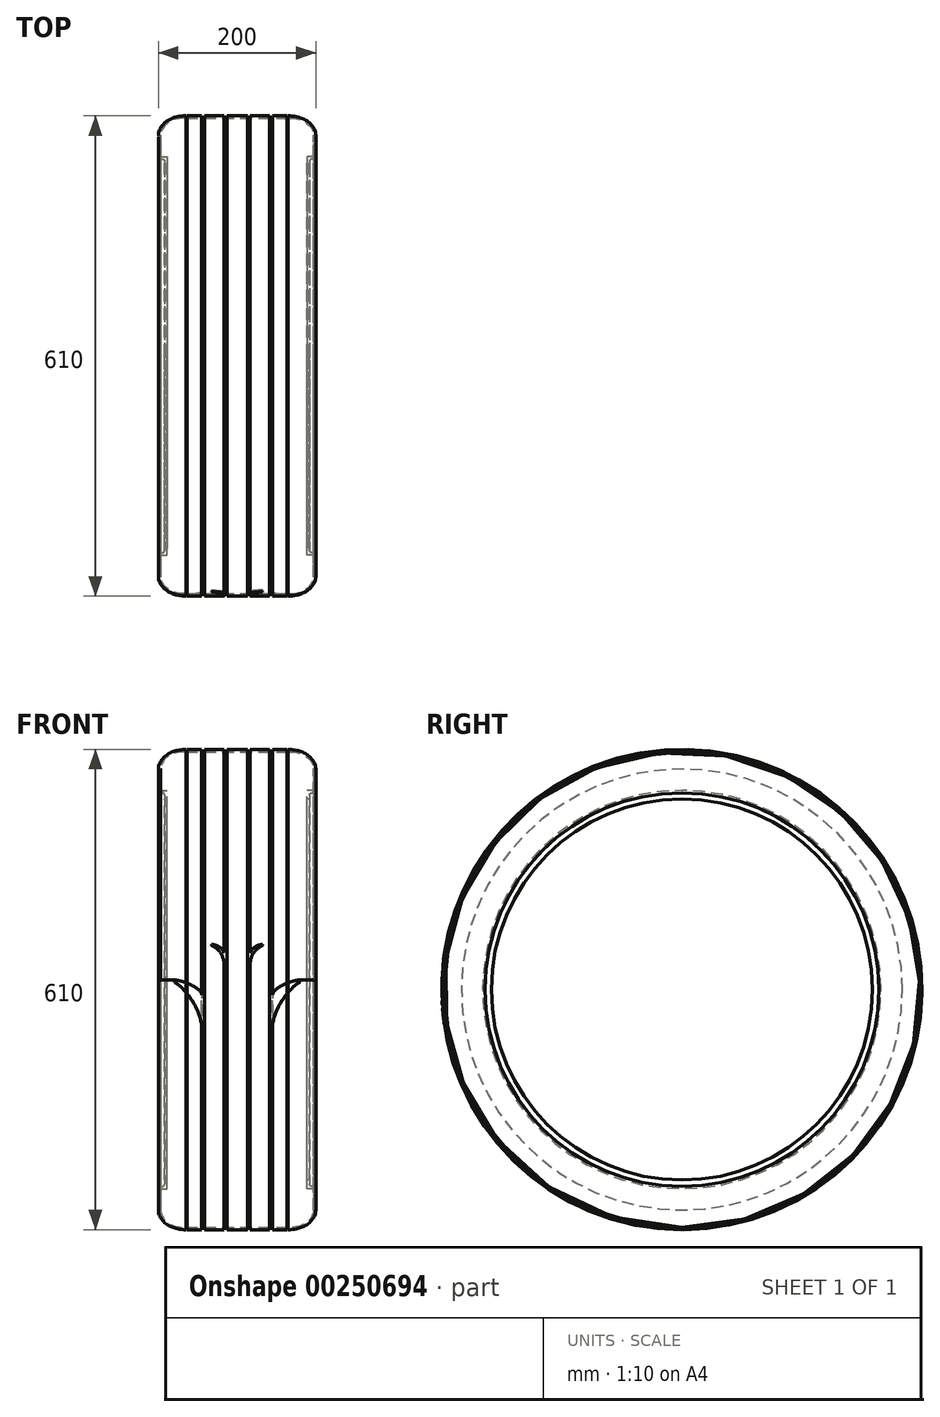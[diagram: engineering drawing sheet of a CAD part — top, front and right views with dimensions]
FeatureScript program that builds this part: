
annotation { "Feature Type Name" : "Feature", "Feature Type Description" : "" }
export const myFeature = defineFeature(function(context is Context, id is Id, definition is map)
    precondition{}
    {
        {
            var Q0;
            Q0=qCreatedBy(makeId("Front.planeOp"),FACE);
            var sketch = newSketch(context, id + "F0", { "sketchPlane" : qUnion([Q0])});
            skLineSegment(sketch, "E0", {"start": v(0, 302) * mm, "end": v(0, 305) * mm});
            skLineSegment(sketch, "E1", {"start": v(0, 305) * mm, "end": v(-65, 305) * mm});
            skLineSegment(sketch, "E2", {"start": v(-92, 250) * mm, "end": v(-100, 250) * mm});
            skLineSegment(sketch, "E3", {"start": v(-100, 250) * mm, "end": v(-100, 280) * mm});
            skFitSpline(sketch, "E4", {"points": [v(-100, 280) * mm, v(-65, 305) * mm], "startDerivative": vector(0, 35.86) * mm, "endDerivative": vector(66.84, 0) * mm});
            skLineSegment(sketch, "E5.0", {"start": v(0, 302) * mm, "end": v(-65, 302) * mm});
            skFitSpline(sketch, "E6.0", {"points": [v(-97, 280) * mm, v(-97, 281.23) * mm, v(-96.67, 283.74) * mm, v(-94.69, 288.83) * mm, v(-89.66, 294.94) * mm, v(-79.59, 300.46) * mm, v(-70.28, 302) * mm, v(-65, 302) * mm]});
            skLineSegment(sketch, "E7.0", {"start": v(-89, 253) * mm, "end": v(-97, 253) * mm});
            skLineSegment(sketch, "E8", {"start": v(-92, 250) * mm, "end": v(-92, 242) * mm});
            skLineSegment(sketch, "E9", {"start": v(-89, 253) * mm, "end": v(-89, 242) * mm});
            skLineSegment(sketch, "E10", {"start": v(-97, 280) * mm, "end": v(-97, 253) * mm});
            skLineSegment(sketch, "E11", {"start": v(-92, 242) * mm, "end": v(-89, 242) * mm});
            skLineSegment(sketch, "E12", {"start": v(0, 0) * mm, "end": v(-100, 0) * mm, "construction": true});
            skSolve(sketch);
        }
        {
            var Q0;
            Q0=makeQuery(id+"F0.imprint","IMPRINT",FACE,{"disambiguationData":[TD([[makeQuery(id+"F0.imprint","IMPRINT",EDGE,{"derivedFrom":sQuery(id+"F0.wireOp",EDGE,"E0")}),1.0]])]});
            var Q1;
            Q1=sQuery(id+"F0.wireOp",EDGE,"E12");
            revolve(context, id + "F1", {"entities" : qUnion([Q0]), "axis" : qUnion([Q1]), "revolveType" : RevolveType.FULL});
        }
        {
            var Q0;
            Q0=qCreatedBy(makeId("Front.planeOp"),FACE);
            var sketch = newSketch(context, id + "F2", { "sketchPlane" : qUnion([Q0])});
            skLineSegment(sketch, "E13.bottom", {"start": v(-16.5, 310) * mm, "end": v(-13, 310) * mm});
            skLineSegment(sketch, "E13.top", {"start": v(-16.5, 303) * mm, "end": v(-13, 303) * mm});
            skLineSegment(sketch, "E13.left", {"start": v(-16.5, 310) * mm, "end": v(-16.5, 303) * mm});
            skLineSegment(sketch, "E13.right", {"start": v(-13, 310) * mm, "end": v(-13, 303) * mm});
            skLineSegment(sketch, "E14.bottom", {"start": v(-45, 310) * mm, "end": v(-41.5, 310) * mm});
            skLineSegment(sketch, "E14.top", {"start": v(-45, 303) * mm, "end": v(-41.5, 303) * mm});
            skLineSegment(sketch, "E14.left", {"start": v(-45, 310) * mm, "end": v(-45, 303) * mm});
            skLineSegment(sketch, "E14.right", {"start": v(-41.5, 310) * mm, "end": v(-41.5, 303) * mm});
            skSolve(sketch);
        }
        {
            var Q0;
            Q0=qSketchRegion(id+"F2",true);
            var Q1;
            Q1=sQuery(id+"F0.wireOp",EDGE,"E12");
            revolve(context, id + "F3", {"operationType" : NewBodyOperationType.REMOVE, "entities" : qUnion([Q0]), "axis" : qUnion([Q1]), "revolveType" : RevolveType.FULL, "oppositeDirection" : true});
        }
        {
            var Q0;
            Q0=qCreatedBy(makeId("Front.planeOp"),FACE);
            cPlane(context, id + "F4", {"entities" : qUnion([Q0]), "cplaneType" : CPlaneType.OFFSET, "offset" : 350 * mm, "width" : 150 * mm, "height" : 150 * mm});
        }
        {
            var Q0;
            Q0=qCreatedBy(id+"F4.planeOp",FACE);
            var sketch = newSketch(context, id + "F5", { "sketchPlane" : qUnion([Q0])});
            skLineSegment(sketch, "E15", {"start": v(-45, -7) * mm, "end": v(-45, -45) * mm});
            skLineSegment(sketch, "E16", {"start": v(-85, 13) * mm, "end": v(-85, 11.5) * mm});
            skFitSpline(sketch, "E17", {"points": [v(-85, 11.5) * mm, v(-45, -45) * mm], "startDerivative": vector(44.6, -10.96) * mm, "endDerivative": vector(11.18, -76.38) * mm});
            skFitSpline(sketch, "E18", {"points": [v(-85, 13) * mm, v(-45, -7) * mm], "startDerivative": vector(39, 0) * mm, "endDerivative": vector(0, -30) * mm});
            skLineSegment(sketch, "E19", {"start": v(-16.5, 32) * mm, "end": v(-16.5, 47) * mm});
            skLineSegment(sketch, "E20", {"start": v(-32.5, 57.5) * mm, "end": v(-32.5, 56) * mm});
            skArc(sketch, "E21", {"start": v(-16.5, 32) * mm, "mid": v(-20.87, 46.42) * mm, "end": v(-32.5, 56) * mm});
            skFitSpline(sketch, "E22", {"points": [v(-16.5, 47) * mm, v(-32.5, 57.5) * mm], "startDerivative": vector(-6, 19.5) * mm, "endDerivative": vector(-15, 0) * mm});
            skSolve(sketch);
        }
        {
            var Q0;
            Q0=makeQuery(id+"F5.imprint","IMPRINT",FACE,{"disambiguationData":[TD([[makeQuery(id+"F5.imprint","IMPRINT",EDGE,{"derivedFrom":sQuery(id+"F5.wireOp",EDGE,"E15")}),-1.0]])]});
            var Q1;
            Q1=makeQuery(id+"F5.imprint","IMPRINT",FACE,{"disambiguationData":[TD([[makeQuery(id+"F5.imprint","IMPRINT",EDGE,{"derivedFrom":sQuery(id+"F5.wireOp",EDGE,"E19")}),1.0]])]});
            var Q2;
            Q2=makeQuery(id+"F3.boolean.opBoolean","COPY",FACE,{"derivedFrom":makeQuery(id+"F3.opRevolve","SWEPT_FACE",FACE,{"disambiguationData":[OSD([sQuery(id+"F2.wireOp",EDGE,"E13.top")])]})});
            extrude(context, id + "F6", {"entities" : qUnion([Q0, Q1]), "operationType" : NewBodyOperationType.REMOVE, "endBound" : BoundingType.UP_TO_SURFACE, "oppositeDirection" : true, "endBoundEntityFace" : qUnion([Q2]), "depth" : 25 * mm});
        }
        {
            var Q0;
            Q0=qCreatedBy(makeId("Front.planeOp"),FACE);
            var sketch = newSketch(context, id + "F7", { "sketchPlane" : qUnion([Q0])});
            skLineSegment(sketch, "E23.bottom", {"start": v(-65, 307.12) * mm, "end": v(-63.5, 307.12) * mm});
            skLineSegment(sketch, "E23.top", {"start": v(-65, 302.12) * mm, "end": v(-63.5, 302.12) * mm});
            skLineSegment(sketch, "E23.left", {"start": v(-65, 307.12) * mm, "end": v(-65, 302.12) * mm});
            skLineSegment(sketch, "E23.right", {"start": v(-63.5, 307.12) * mm, "end": v(-63.5, 302.12) * mm});
            skSolve(sketch);
        }
        {
            var Q0;
            Q0=qSketchRegion(id+"F7",true);
            var Q1;
            Q1=sQuery(id+"F0.wireOp",EDGE,"E12");
            revolve(context, id + "F8", {"operationType" : NewBodyOperationType.REMOVE, "entities" : qUnion([Q0]), "axis" : qUnion([Q1]), "revolveType" : RevolveType.FULL, "oppositeDirection" : true});
        }
        {
            var Q0;
            Q0=makeQuery(id+"F1.opRevolve","SWEPT_EDGE",EDGE,{"disambiguationData":[OSD([sQuery(id+"F0.wireOp",EDGE,"E2"),sQuery(id+"F0.wireOp",EDGE,"E8")])]});
            var Q1;
            Q1=makeQuery(id+"F1.opRevolve","SWEPT_EDGE",EDGE,{"disambiguationData":[OSD([sQuery(id+"F0.wireOp",EDGE,"E2"),sQuery(id+"F0.wireOp",EDGE,"E3")])]});
            fillet(context, id + "F9", {"entities" : qUnion([Q0, Q1]), "radius" : 3 * mm, "tangentPropagation" : true, "allowEdgeOverflow" : false});
        }
        {
            var Q0;
            Q0=makeQuery(id+"F1.opRevolve","SWEPT_BODY",BODY,{"disambiguationData":[OSD([sQuery(id+"F0.wireOp",EDGE,"E0"),sQuery(id+"F0.wireOp",EDGE,"E1"),sQuery(id+"F0.wireOp",EDGE,"E2"),sQuery(id+"F0.wireOp",EDGE,"E3"),sQuery(id+"F0.wireOp",EDGE,"E4"),sQuery(id+"F0.wireOp",EDGE,"E5.0"),sQuery(id+"F0.wireOp",EDGE,"E6.0"),sQuery(id+"F0.wireOp",EDGE,"E7.0"),sQuery(id+"F0.wireOp",EDGE,"E8"),sQuery(id+"F0.wireOp",EDGE,"E9"),sQuery(id+"F0.wireOp",EDGE,"E10"),sQuery(id+"F0.wireOp",EDGE,"E11")])]});
            var Q1;
            Q1=qCreatedBy(makeId("Right.planeOp"),FACE);
            mirror(context, id + "F10", {"operationType" : NewBodyOperationType.ADD, "entities" : qUnion([Q0]), "mirrorPlane" : qUnion([Q1])});
        }
    });
